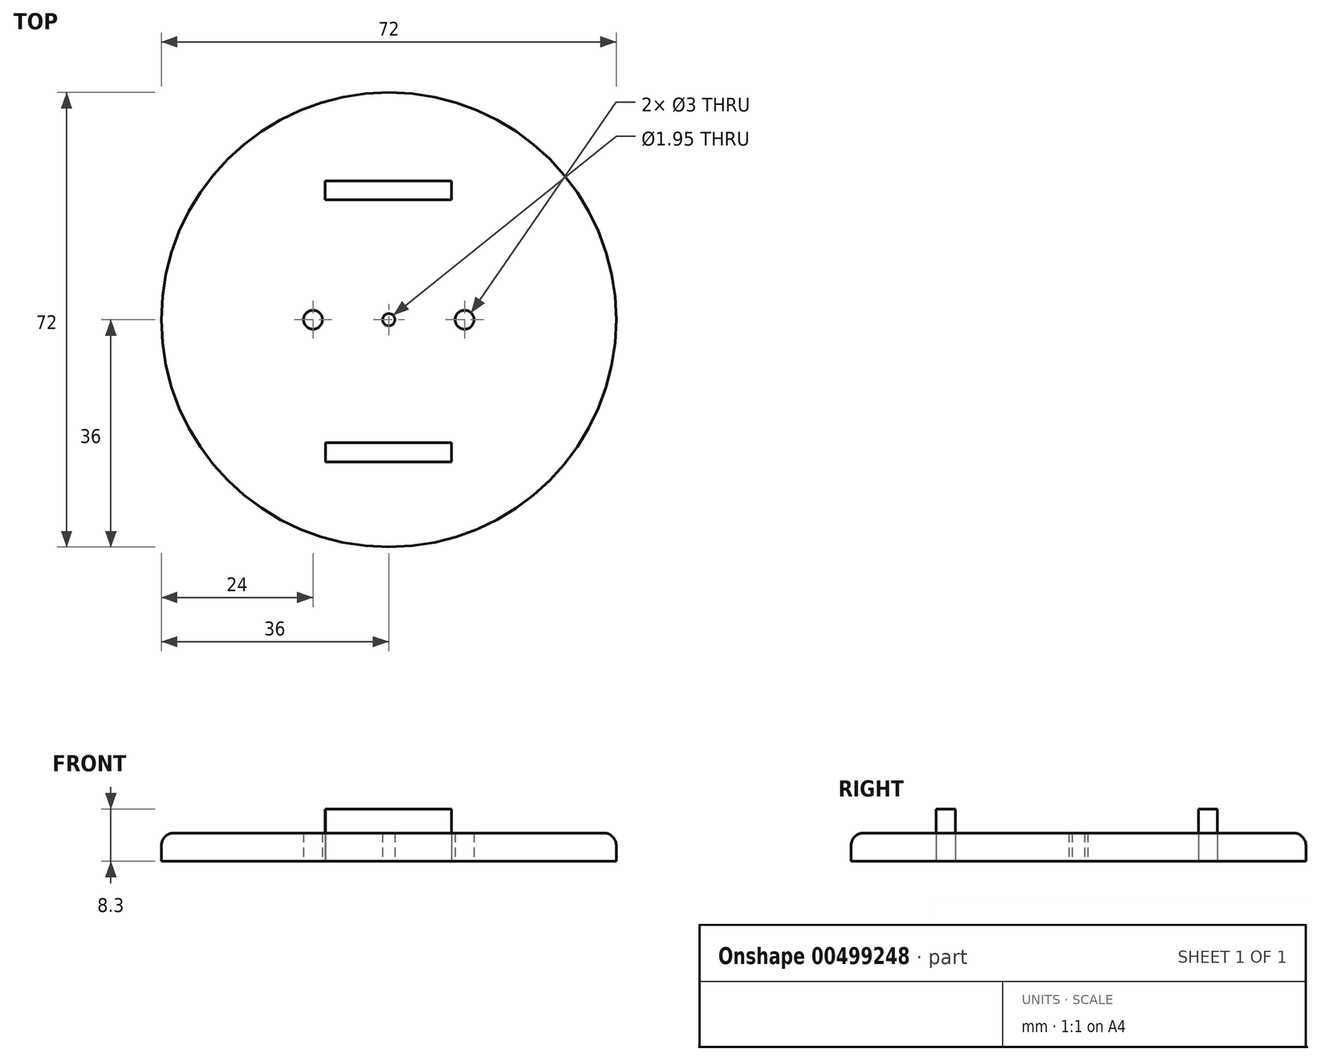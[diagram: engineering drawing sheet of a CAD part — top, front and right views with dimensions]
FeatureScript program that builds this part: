
annotation { "Feature Type Name" : "Feature", "Feature Type Description" : "" }
export const myFeature = defineFeature(function(context is Context, id is Id, definition is map)
    precondition{}
    {
        {
            var Q0;
            Q0=qCreatedBy(makeId("Top.planeOp"),FACE);
            var sketch = newSketch(context, id + "F0", { "sketchPlane" : qUnion([Q0])});
            skCircle(sketch, "E0", {"center": v(0, 0) * mm, "radius": 36 * mm});
            skSolve(sketch);
        }
        {
            var Q0;
            Q0=makeQuery(id+"F0.imprint","IMPRINT",FACE,{"disambiguationData":[TD([[makeQuery(id+"F0.imprint","IMPRINT",EDGE,{"derivedFrom":sQuery(id+"F0.wireOp",EDGE,"E0")}),1.0]])]});
            extrude(context, id + "F1", {"entities" : qUnion([Q0]), "depth" : 4.5 * mm});
        }
        {
            var Q0;
            Q0=makeQuery(id+"F1.opExtrude","CAP_EDGE",EDGE,{"disambiguationData":[OSD([sQuery(id+"F0.wireOp",EDGE,"E0")])],"isStart":false});
            fillet(context, id + "F2", {"entities" : qUnion([Q0]), "radius" : 2 * mm, "tangentPropagation" : true, "allowEdgeOverflow" : false});
        }
        {
            var Q0;
            Q0=qCreatedBy(makeId("Top.planeOp"),FACE);
            var sketch = newSketch(context, id + "F3", { "sketchPlane" : qUnion([Q0])});
            skCircle(sketch, "E1", {"center": v(0, 0) * mm, "radius": 0.97 * mm});
            skSolve(sketch);
        }
        {
            var Q0;
            Q0 = qSketchRegion(id + "F3", true);
            extrude(context, id + "F4", {"entities" : qUnion([Q0]), "operationType" : NewBodyOperationType.REMOVE, "depth" : 12.4 * mm});
        }
        {
            var Q0;
            Q0=qCreatedBy(makeId("Top.planeOp"),FACE);
            var sketch = newSketch(context, id + "F5", { "sketchPlane" : qUnion([Q0])});
            skCircle(sketch, "E2", {"center": v(-12, 0) * mm, "radius": 1.5 * mm});
            skCircle(sketch, "E3", {"center": v(12, 0) * mm, "radius": 1.5 * mm});
            skSolve(sketch);
        }
        {
            var Q0;
            Q0 = qSketchRegion(id + "F5", true);
            extrude(context, id + "F6", {"entities" : qUnion([Q0]), "operationType" : NewBodyOperationType.REMOVE, "depth" : 65.8 * mm});
        }
        {
            var Q0;
            Q0=qCreatedBy(makeId("Top.planeOp"),FACE);
            var sketch = newSketch(context, id + "F7", { "sketchPlane" : qUnion([Q0])});
            skLineSegment(sketch, "E4", {"start": v(0, -19.47) * mm, "end": v(-10, -19.47) * mm});
            skLineSegment(sketch, "E5.bottom", {"start": v(-10, -19.47) * mm, "end": v(9.92, -19.47) * mm});
            skLineSegment(sketch, "E5.top", {"start": v(-10, -22.56) * mm, "end": v(9.92, -22.56) * mm});
            skLineSegment(sketch, "E5.left", {"start": v(-10, -19.47) * mm, "end": v(-10, -22.56) * mm});
            skLineSegment(sketch, "E5.right", {"start": v(9.92, -19.47) * mm, "end": v(9.92, -22.56) * mm});
            skSolve(sketch);
        }
        {
            var Q0;
            Q0 = qSketchRegion(id + "F7", true);
            extrude(context, id + "F8", {"entities" : qUnion([Q0]), "depth" : 8.3 * mm});
        }
        {
            var Q0;
            Q0=qCreatedBy(makeId("Top.planeOp"),FACE);
            var sketch = newSketch(context, id + "F9", { "sketchPlane" : qUnion([Q0])});
            skLineSegment(sketch, "E6", {"start": v(0, 19) * mm, "end": v(9.93, 19) * mm});
            skLineSegment(sketch, "E7.bottom", {"start": v(9.93, 19) * mm, "end": v(-10.07, 19) * mm});
            skLineSegment(sketch, "E7.top", {"start": v(9.93, 22) * mm, "end": v(-10.07, 22) * mm});
            skLineSegment(sketch, "E7.left", {"start": v(9.93, 19) * mm, "end": v(9.93, 22) * mm});
            skLineSegment(sketch, "E7.right", {"start": v(-10.07, 19) * mm, "end": v(-10.07, 22) * mm});
            skSolve(sketch);
        }
        {
            var Q0;
            Q0 = qSketchRegion(id + "F9", true);
            extrude(context, id + "F10", {"entities" : qUnion([Q0]), "depth" : 8.3 * mm});
        }
    });
